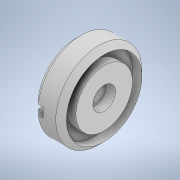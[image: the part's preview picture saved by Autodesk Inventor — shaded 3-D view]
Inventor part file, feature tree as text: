
AUTODESK INVENTOR PART (.ipt)
format: ipt  version: 2022 (Build 260153000, 153)  size: 167,424 bytes
history: native  units: mm
features: sketch x4, revolve x2, other x1, hole x1, extrude x1
ambient origin geometry x8: Origin, YZ Plane, XZ Plane, XY Plane, X Axis, Y Axis, Z Axis, Center Point
bodies: Body1 (feature_tree)
feature tree (9):
  other  "Твердое тело1"
  revolve  "Вращение1"
  revolve  "Вращение2"
  hole  "Отверстие1"  [1 undecoded]
  extrude  "Выдавливание2"  Depth=4.0mm
  sketch  "Эскиз1"
  sketch  "Эскиз2"
  sketch  "Эскиз4"
  sketch  "Эскиз5"
note: 1 required parameter value undecoded (feature->parameter linkage not recoverable at this tier; creation-order binding heuristic only, values carry confidence <= 0.55)
